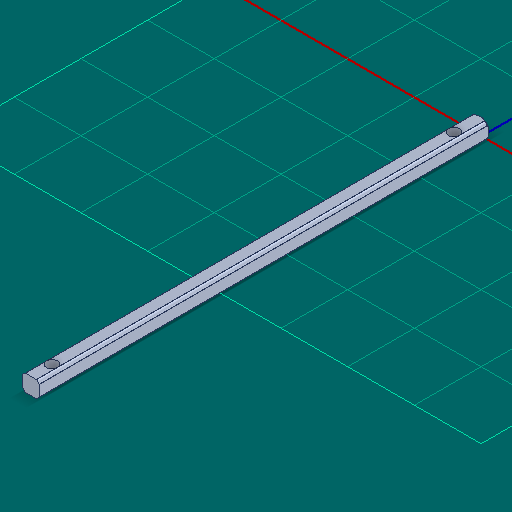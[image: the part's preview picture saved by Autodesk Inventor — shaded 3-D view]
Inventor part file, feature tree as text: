
AUTODESK INVENTOR PART (.ipt)
format: ipt  version: 2025 (Build 290162000, 162)  size: 207,360 bytes
history: native  units: in
note: dims shown in document units (in); Inventor stores cm internally (conversion verified against a paired STEP export)
features: extrude x4, sketch x4, thicken_offset x1, projected_geometry x1, other x1
ambient origin geometry x8: Origin, YZ Plane, XZ Plane, XY Plane, X Axis, Y Axis, Z Axis, Center Point
bodies: Solid1 (feature_tree)
feature tree (11):
  extrude  "Extrusion1"  Depth=12.1875in
  thicken_offset  "Thicken1"
  extrude  "Extrusion2"  Depth=17.125in
  extrude  "Extrusion3"  Depth=6.0268in
  extrude  "Extrusion4"  Depth=1.0in TaperAngle=0.0deg
  sketch  "Sketch2"  dims[d0=0.0625in d1=0.0in d2=12.1875in]
  sketch  "Sketch3"  dims[d3=12.125in d4=17.125in]
  sketch  "Sketch4"  dims[d5=0.0in d6=6.0268in]
  sketch  "Sketch5"  dims[d8=0.25in d9=1.0in d10=0.0in d11=0.25in d12=0.0in]
  projected_geometry  "Projected Loop1"
  other  "Cut-Revolve3"
